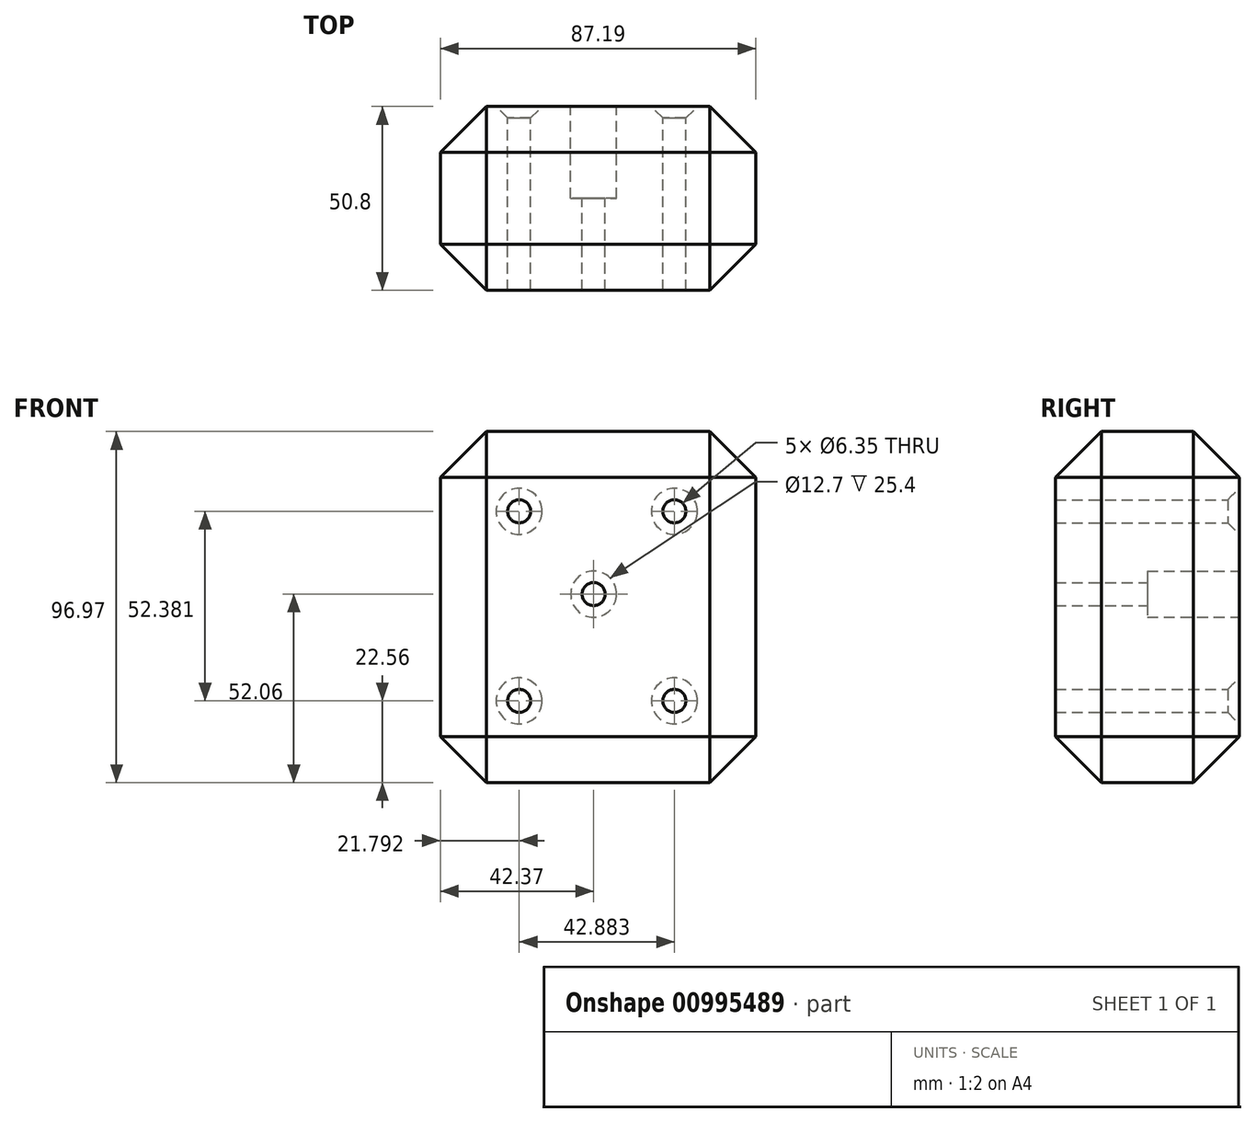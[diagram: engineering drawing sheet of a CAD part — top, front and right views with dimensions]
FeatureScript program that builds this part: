
annotation { "Feature Type Name" : "Feature", "Feature Type Description" : "" }
export const myFeature = defineFeature(function(context is Context, id is Id, definition is map)
    precondition{}
    {
        {
            var Q0;
            Q0=qCreatedBy(makeId("Front.planeOp"),FACE);
            var sketch = newSketch(context, id + "F0", { "sketchPlane" : qUnion([Q0])});
            skLineSegment(sketch, "E0.bottom", {"start": v(-42.37, 44.91) * mm, "end": v(44.82, 44.91) * mm});
            skLineSegment(sketch, "E0.top", {"start": v(-42.37, -52.06) * mm, "end": v(44.82, -52.06) * mm});
            skLineSegment(sketch, "E0.left", {"start": v(-42.37, 44.91) * mm, "end": v(-42.37, -52.06) * mm});
            skLineSegment(sketch, "E0.right", {"start": v(44.82, 44.91) * mm, "end": v(44.82, -52.06) * mm});
            skSolve(sketch);
        }
        {
            var Q0;
            Q0 = qSketchRegion(id + "F0", true);
            var Q1;
            Q1=makeQuery(id+"FKywvfNQ1IWonHh_0.imprint","IMPRINT",FACE,{"disambiguationData":[TD([[makeQuery(id+"FKywvfNQ1IWonHh_0.imprint","IMPRINT",EDGE,{"derivedFrom":sQuery(id+"FKywvfNQ1IWonHh_0.wireOp",EDGE,"283a6448-f5a7-4e8e-8a68-6b8de3328e7f.bottom")}),1.0]])]});
            extrude(context, id + "F1", {"entities" : qUnion([Q0, Q1]), "depth" : 50.8 * mm, "offsetDistance" : 25.4 * mm});
        }
        {
            var Q0;
            Q0=qCreatedBy(makeId("Front.planeOp"),FACE);
            var sketch = newSketch(context, id + "F2", { "sketchPlane" : qUnion([Q0])});
            skLineSegment(sketch, "E1.bottom", {"start": v(-12.7, -12.7) * mm, "end": v(12.7, -12.7) * mm});
            skLineSegment(sketch, "E1.top", {"start": v(-12.7, 12.7) * mm, "end": v(12.7, 12.7) * mm});
            skLineSegment(sketch, "E1.left", {"start": v(-12.7, -12.7) * mm, "end": v(-12.7, 12.7) * mm});
            skLineSegment(sketch, "E1.right", {"start": v(12.7, -12.7) * mm, "end": v(12.7, 12.7) * mm});
            skPoint(sketch, "E1.middle", {"position": v(0, 0) * mm});
            skSolve(sketch);
        }
        {
            var Q0;
            Q0=sQuery(id+"F2.wireOp",VERTEX,"E1.middle");
            var Q1;
            Q1=makeQuery(id+"F1.opExtrude","SWEPT_BODY",BODY,{"disambiguationData":[OSD([sQuery(id+"F0.wireOp",EDGE,"E0.bottom"),sQuery(id+"F0.wireOp",EDGE,"E0.top"),sQuery(id+"F0.wireOp",EDGE,"E0.left"),sQuery(id+"F0.wireOp",EDGE,"E0.right")])]});
            hole(context, id + "F3", {"style" : HoleStyle.C_BORE, "endStyle" : HoleEndStyle.THROUGH, "oppositeDirection" : true, "holeDiameter" : 6.35 * mm, "cBoreDiameter" : 12.7 * mm, "cBoreDepth" : 25.4 * mm, "majorDiameter" : 6.35 * mm, "isTappedThrough" : true, "tappedDepth" : 12.7 * mm, "tapClearance" : 3, "locations" : qUnion([Q0]), "scope" : qUnion([Q1])});
        }
        {
            var Q0;
            Q0=qCreatedBy(makeId("Front.planeOp"),FACE);
            var sketch = newSketch(context, id + "F4", { "sketchPlane" : qUnion([Q0])});
            skPoint(sketch, "E2", {"position": v(0, 0) * mm});
            skPoint(sketch, "E3", {"position": v(0, -29.5) * mm});
            skPoint(sketch, "E4", {"position": v(22.3, -29.5) * mm});
            skPoint(sketch, "E5", {"position": v(22.3, 22.88) * mm});
            skPoint(sketch, "E6", {"position": v(-20.58, 22.88) * mm});
            skPoint(sketch, "E7", {"position": v(-20.58, -29.5) * mm});
            skSolve(sketch);
        }
        {
            var Q0;
            Q0=sQuery(id+"F4.wireOp",VERTEX,"E5");
            var Q1;
            Q1=sQuery(id+"F4.wireOp",VERTEX,"E6");
            var Q2;
            Q2=sQuery(id+"F4.wireOp",VERTEX,"E7");
            var Q3;
            Q3=sQuery(id+"F4.wireOp",VERTEX,"E4");
            var Q4;
            Q4=makeQuery(id+"F1.opExtrude","SWEPT_BODY",BODY,{"disambiguationData":[OSD([sQuery(id+"F0.wireOp",EDGE,"E0.bottom"),sQuery(id+"F0.wireOp",EDGE,"E0.top"),sQuery(id+"F0.wireOp",EDGE,"E0.left"),sQuery(id+"F0.wireOp",EDGE,"E0.right")])]});
            hole(context, id + "F5", {"style" : HoleStyle.C_SINK, "endStyle" : HoleEndStyle.THROUGH, "oppositeDirection" : true, "holeDiameter" : 6.35 * mm, "cSinkDiameter" : 12.7 * mm, "cSinkAngle" : 90 * degree, "majorDiameter" : 6.35 * mm, "isTappedThrough" : true, "tappedDepth" : 12.7 * mm, "tapClearance" : 3, "locations" : qUnion([Q0, Q1, Q2, Q3]), "scope" : qUnion([Q4])});
        }
        {
            var Q0;
            Q0=makeQuery(id+"F1.opExtrude","SWEPT_EDGE",EDGE,{"disambiguationData":[OSD([sQuery(id+"F0.wireOp",EDGE,"E0.top"),sQuery(id+"F0.wireOp",EDGE,"E0.left")])]});
            var Q1;
            Q1=makeQuery(id+"F1.opExtrude","SWEPT_FACE",FACE,{"disambiguationData":[OSD([sQuery(id+"F0.wireOp",EDGE,"E0.top")])]});
            var Q2;
            Q2=makeQuery(id+"F1.opExtrude","SWEPT_FACE",FACE,{"disambiguationData":[OSD([sQuery(id+"F0.wireOp",EDGE,"E0.left")])]});
            var Q3;
            Q3=makeQuery(id+"F1.opExtrude","SWEPT_FACE",FACE,{"disambiguationData":[OSD([sQuery(id+"F0.wireOp",EDGE,"E0.right")])]});
            var Q4;
            Q4=makeQuery(id+"F1.opExtrude","SWEPT_FACE",FACE,{"disambiguationData":[OSD([sQuery(id+"F0.wireOp",EDGE,"E0.bottom")])]});
            chamfer(context, id + "F6", {"entities" : qUnion([Q0, Q1, Q2, Q3, Q4]), "width" : 12.7 * mm, "tangentPropagation" : true});
        }
    });
